# Revit family: Light-Street-Vizona-Zora ST Series1
name_source: partatom
category: Lighting Fixtures
revit_build: Autodesk Revit 2018 (Build: 20190510_1515(x64)
units: mm (PartAtom-declared; Revit-internal decimal feet)

## family parameters
Cut with Voids When Loaded = No
Host = Face
Light Source = Yes
OmniClass Number = 23.80.70.00
OmniClass Title = Lighting
Part Type = Normal
Room Calculation Point = No
Round Connector Dimension = Use Diameter
Shared = Yes

## types (7) — shared parameters
Assembly Code = D5020
Color Filter = 16777215
Dimming = Non Dimming
Dimming Lamp Color Temperature Shift = <None>
LED Module1 = Yes
Length_ANZRS = 400 mm  [stored 1.31234 ft]
Light Source = Plastic-Light Source-On
Manufacturer = Vizona
ModifiedIssue_ANZRS = 20190926 $
NumberOfPoles_ANZRS = 1
Offset1 = 244 mm  [stored 0.800525 ft]
Offset3 = -40 mm  [stored -0.131234 ft]
Offset4 = 200 mm  [stored 0.656168 ft]
PowerFactor_ANZRS = 1
SupplyFrequency = 50 Hz
Tilt Angle = 0.00°
URL = http://www.vizona.com.au
Void Offset = 50 mm  [stored 0.164042 ft]
Voltage_ANZRS = 240 V
Width_ANZRS = 100 mm  [stored 0.328084 ft]
zero-valued in all types: Default Elevation

## per-type parameters (varying)
| type | Apparent Load | ApparentCurrent_ANZRS | Description | Height_ANZRS | LED Extension | LED Glass | LED Module2 | LED Module3 | Lamp | Logo | Material_ANZRS | Model | Offset2 | Photometric Web File | Type Selector | Vents | Wattage_ANZRS | WeightNet_ANZRS |
| Zora Small ST Series (90W) | 90 VA | 0 A | Zora Small ST Series 90W | 565 mm  [stored 1.85367 ft] | 160 mm  [stored 0.524934 ft] | Glass-Opaque-Black | No | No | 45 LEDs | Metal-Aluminium-Powdercoated-Black-Satin | Metal-Aluminium-Powdercoated-Grey-Satin | ZSST90W | 404 mm | [QAV-0717-0168] Vizona_Street Light (Vizona Zora ST90).ies | 0 | Metal-Aluminium-Powdercoated-Grey-Vents | 90 VA | 10.00 kg |
| Zora Large ST Series (300W) | 300 VA | 1 A | Zora Large ST Series 300W | 883 mm  [stored 2.89698 ft] | 480 mm  [stored 1.5748 ft] | <By Category> | Yes | Yes | 135 LEDs | <By Category> | <By Category> | ZLST300W | 724 mm  [stored 2.37533 ft] | [QAV-0917-0099] OLE_Street Light (OLE Dura ST300).ies | 6 | <By Category> | 300 VA | 16.50 kg |
| Zora Large ST Series (270W) | 270 VA | 1 A | Zora Large ST Series 270W | 883 mm  [stored 2.89698 ft] | 480 mm  [stored 1.5748 ft] | <By Category> | Yes | Yes | 135 LEDs | <By Category> | <By Category> | ZLST270W | 724 mm  [stored 2.37533 ft] | [QAV-0717-0173] Vizona_Street Light (Vizona Zora ST270).ies | 5 | <By Category> | 270 VA | 16.50 kg |
| Zora Medium ST Series (240W) | 240 VA | 1 A | Zora Medium ST Series 240W | 725 mm  [stored 2.37861 ft] | 320 mm  [stored 1.04987 ft] | <By Category> | Yes | No | 90 LEDs | <By Category> | <By Category> | ZMST240W | 564 mm  [stored 1.85039 ft] | [QAV-0717-0172] Vizona_Street Light (Vizona Zora ST240).ies | 4 | <By Category> | 240 VA | 13.00 kg |
| Zora Medium ST Series (180W) | 180 VA | 1 A | Zora Medium ST Series 180W | 725 mm  [stored 2.37861 ft] | 320 mm  [stored 1.04987 ft] | <By Category> | Yes | No | 90 LEDs | <By Category> | <By Category> | ZMST180W | 564 mm  [stored 1.85039 ft] | [QAV-0717-0171] Vizona_Street Light (Vizona Zora ST180).ies | 3 | <By Category> | 180 VA | 13.00 kg |
| Zora Medium ST Series (150W) | 150 VA | 1 A | Zora Medium ST Series 150W | 725 mm  [stored 2.37861 ft] | 320 mm  [stored 1.04987 ft] | <By Category> | Yes | No | 90 LEDs | <By Category> | <By Category> | ZMST150W | 564 mm  [stored 1.85039 ft] | [QAV-0717-0170] Vizona_Street Light (Vizona Zora ST150).ies | 2 | <By Category> | 150 VA | 13.00 kg |
| Zora Small ST Series (120W) | 120 VA | 1 A | Zora Small ST Series 120W | 565 mm  [stored 1.85367 ft] | 160 mm  [stored 0.524934 ft] | <By Category> | No | No | 45 LEDs | <By Category> | <By Category> | ZSST120W | 404 mm | [QAV-0717-0169] Vizona_Street Light (Vizona Zora ST120).ies | 1 | <By Category> | 120 VA | 10.00 kg |

note: [stored X ft] marks values corroborated as IEEE doubles in the binary element streams (Revit-internal decimal feet)

## geometry (parser evidence)
native form markers: Sweep x7
no freeform markers — native parametric forms only
